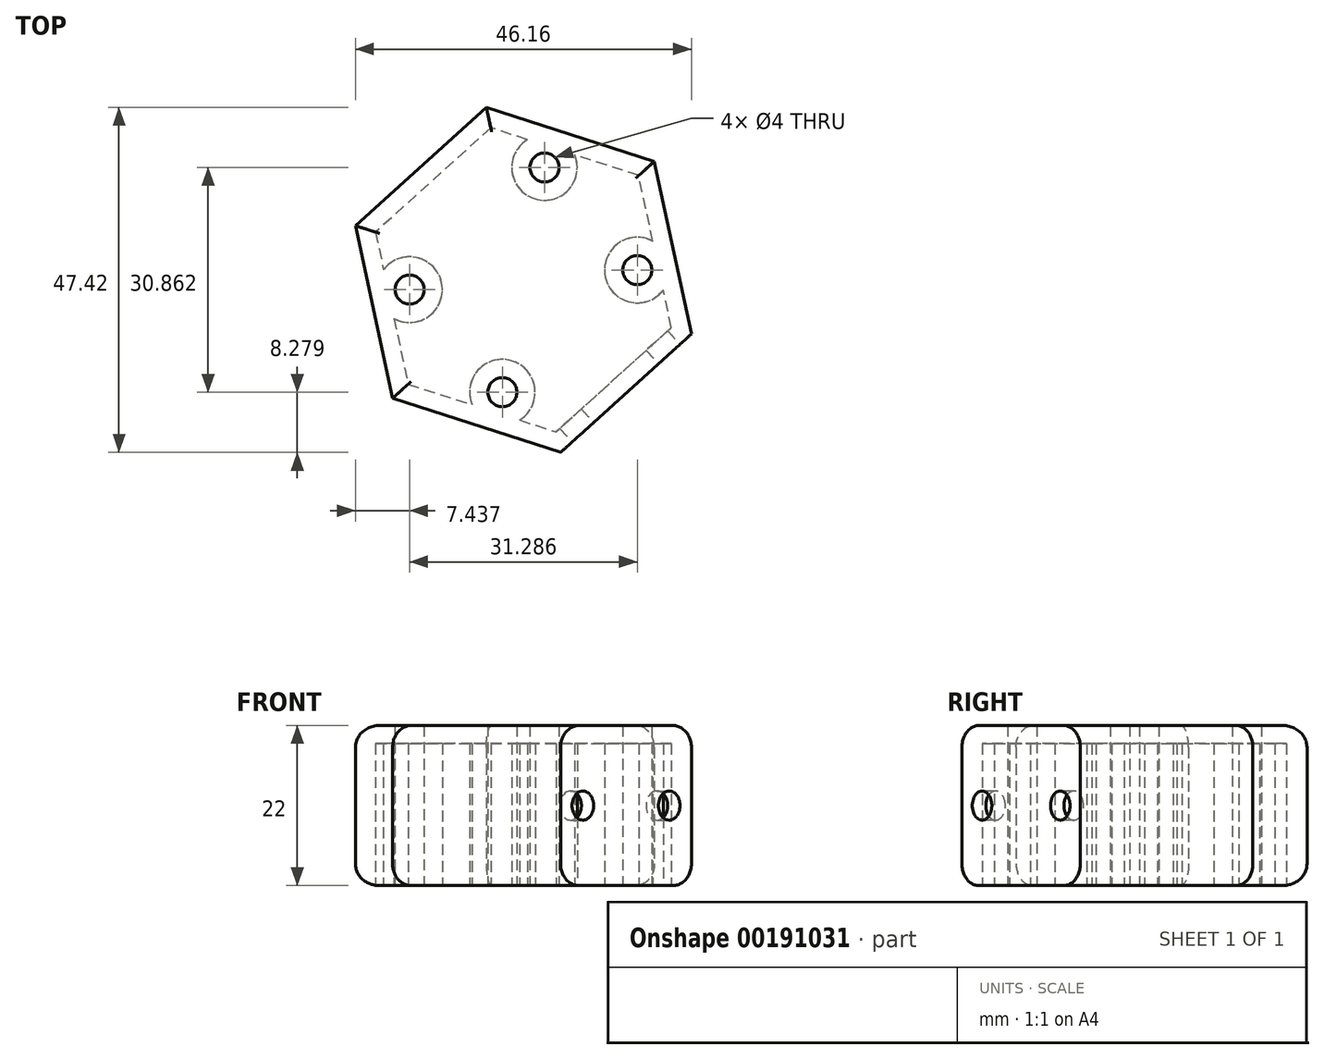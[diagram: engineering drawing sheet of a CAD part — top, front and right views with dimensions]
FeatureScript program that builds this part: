
annotation { "Feature Type Name" : "Feature", "Feature Type Description" : "" }
export const myFeature = defineFeature(function(context is Context, id is Id, definition is map)
    precondition{}
    {
        {
            var Q0;
            Q0=qCreatedBy(makeId("Top.planeOp"),FACE);
            var sketch = newSketch(context, id + "F0", { "sketchPlane" : qUnion([Q0])});
            skCircle(sketch, "E0.cCircle", {"center": v(0, 0) * mm, "radius": 21 * mm, "construction": true});
            skLineSegment(sketch, "E0.0", {"start": v(23.08, -7.44) * mm, "end": v(5.1, -23.7) * mm});
            skLineSegment(sketch, "E0.1", {"start": v(5.1, -23.7) * mm, "end": v(-17.98, -16.27) * mm});
            skLineSegment(sketch, "E0.2", {"start": v(-17.98, -16.27) * mm, "end": v(-23.08, 7.44) * mm});
            skLineSegment(sketch, "E0.3", {"start": v(-23.08, 7.44) * mm, "end": v(-5.1, 23.7) * mm});
            skLineSegment(sketch, "E0.4", {"start": v(-5.1, 23.7) * mm, "end": v(17.98, 16.27) * mm});
            skLineSegment(sketch, "E0.5", {"start": v(17.98, 16.27) * mm, "end": v(23.08, -7.44) * mm});
            skPoint(sketch, "E0.0.midPoint", {"position": v(14.09, -15.57) * mm});
            skLineSegment(sketch, "E1", {"start": v(17.98, 16.27) * mm, "end": v(-17.98, -16.27) * mm, "construction": true});
            skLineSegment(sketch, "E2", {"start": v(14.09, -15.57) * mm, "end": v(-14.09, 15.57) * mm, "construction": true});
            skPoint(sketch, "E3", {"position": v(-15.64, -1.34) * mm});
            skPoint(sketch, "E4.MirrorP", {"position": v(2.9, 15.43) * mm});
            skPoint(sketch, "E5.MirrorP", {"position": v(-2.9, -15.43) * mm});
            skPoint(sketch, "E6.MirrorP", {"position": v(15.64, 1.34) * mm});
            skSolve(sketch);
        }
        {
            var Q0;
            Q0=makeQuery(id+"F0.imprint","IMPRINT",FACE,{"disambiguationData":[TD([[makeQuery(id+"F0.imprint","IMPRINT",EDGE,{"derivedFrom":sQuery(id+"F0.wireOp",EDGE,"E0.0")}),-1.0]])]});
            extrude(context, id + "F1", {"entities" : qUnion([Q0]), "depth" : 22 * mm});
        }
        {
            var Q0;
            Q0=sQuery(id+"F0.wireOp",VERTEX,"E4.MirrorP");
            var Q1;
            Q1=sQuery(id+"F0.wireOp",VERTEX,"E3");
            var Q2;
            Q2=sQuery(id+"F0.wireOp",VERTEX,"E5.MirrorP");
            var Q3;
            Q3=sQuery(id+"F0.wireOp",VERTEX,"E6.MirrorP");
            var Q4;
            Q4=makeQuery(id+"F1.opExtrude","SWEPT_BODY",BODY,{"disambiguationData":[OSD([sQuery(id+"F0.wireOp",EDGE,"E0.0"),sQuery(id+"F0.wireOp",EDGE,"E0.1"),sQuery(id+"F0.wireOp",EDGE,"E0.2"),sQuery(id+"F0.wireOp",EDGE,"E0.3"),sQuery(id+"F0.wireOp",EDGE,"E0.4"),sQuery(id+"F0.wireOp",EDGE,"E0.5")])]});
            hole(context, id + "F2", {"style" : HoleStyle.SIMPLE, "endStyle" : HoleEndStyle.THROUGH, "oppositeDirection" : true, "holeDiameter" : 4 * mm, "locations" : qUnion([Q0, Q1, Q2, Q3]), "scope" : qUnion([Q4]), "isTappedThrough" : true});
        }
        {
            var Q0;
            Q0=makeQuery(id+"F1.opExtrude","CAP_FACE",FACE,{"disambiguationData":[OSD([sQuery(id+"F0.wireOp",EDGE,"E0.0"),sQuery(id+"F0.wireOp",EDGE,"E0.1"),sQuery(id+"F0.wireOp",EDGE,"E0.2"),sQuery(id+"F0.wireOp",EDGE,"E0.3"),sQuery(id+"F0.wireOp",EDGE,"E0.4"),sQuery(id+"F0.wireOp",EDGE,"E0.5")])],"isStart":true});
            var Q1;
            Q1=makeQuery(id+"F2.hole-0.boolean.opBoolean","COPY",FACE,{"derivedFrom":makeQuery(id+"F2.hole-0.opRevolve","SWEPT_FACE",FACE,{"disambiguationData":[OSD([sQuery(id+"F2.hole-0.sketch.wireOp",EDGE,"core_line_2")])]})});
            var Q2;
            Q2=makeQuery(id+"F2.hole-3.boolean.opBoolean","COPY",FACE,{"derivedFrom":makeQuery(id+"F2.hole-3.opRevolve","SWEPT_FACE",FACE,{"disambiguationData":[OSD([sQuery(id+"F2.hole-3.sketch.wireOp",EDGE,"core_line_2")])]})});
            var Q3;
            Q3=makeQuery(id+"F2.hole-2.boolean.opBoolean","COPY",FACE,{"derivedFrom":makeQuery(id+"F2.hole-2.opRevolve","SWEPT_FACE",FACE,{"disambiguationData":[OSD([sQuery(id+"F2.hole-2.sketch.wireOp",EDGE,"core_line_2")])]})});
            var Q4;
            Q4=makeQuery(id+"F2.hole-1.boolean.opBoolean","COPY",FACE,{"derivedFrom":makeQuery(id+"F2.hole-1.opRevolve","SWEPT_FACE",FACE,{"disambiguationData":[OSD([sQuery(id+"F2.hole-1.sketch.wireOp",EDGE,"core_line_2")])]})});
            shell(context, id + "F3", {"entities" : qUnion([Q0, Q1, Q2, Q3, Q4]), "thickness" : 2.5 * mm});
        }
        {
            var Q0;
            Q0=makeQuery(id+"F1.opExtrude","SWEPT_FACE",FACE,{"disambiguationData":[OSD([sQuery(id+"F0.wireOp",EDGE,"E0.0")])]});
            var sketch = newSketch(context, id + "F4", { "sketchPlane" : qUnion([Q0])});
            skLineSegment(sketch, "E7.bottom", {"start": v(-12.12, 22) * mm, "end": v(12.12, 22) * mm});
            skLineSegment(sketch, "E7.top", {"start": v(-12.12, 0) * mm, "end": v(12.12, 0) * mm});
            skLineSegment(sketch, "E7.left", {"start": v(-12.12, 22) * mm, "end": v(-12.12, 0) * mm});
            skLineSegment(sketch, "E7.right", {"start": v(12.12, 22) * mm, "end": v(12.12, 0) * mm});
            skLineSegment(sketch, "E8", {"start": v(0, 22) * mm, "end": v(0, 0) * mm, "construction": true});
            skLineSegment(sketch, "E9", {"start": v(-12.12, 11) * mm, "end": v(12.12, 11) * mm, "construction": true});
            skPoint(sketch, "E10", {"position": v(-8, 11) * mm});
            skPoint(sketch, "E11.MirrorP", {"position": v(8, 11) * mm});
            skSolve(sketch);
        }
        {
            var Q0;
            Q0=makeQuery(id+"F1.opExtrude","CAP_EDGE",EDGE,{"disambiguationData":[OSD([sQuery(id+"F0.wireOp",EDGE,"E0.1")])],"isStart":false});
            var Q1;
            Q1=makeQuery(id+"F1.opExtrude","CAP_EDGE",EDGE,{"disambiguationData":[OSD([sQuery(id+"F0.wireOp",EDGE,"E0.2")])],"isStart":false});
            var Q2;
            Q2=makeQuery(id+"F1.opExtrude","CAP_EDGE",EDGE,{"disambiguationData":[OSD([sQuery(id+"F0.wireOp",EDGE,"E0.3")])],"isStart":false});
            var Q3;
            Q3=makeQuery(id+"F1.opExtrude","CAP_EDGE",EDGE,{"disambiguationData":[OSD([sQuery(id+"F0.wireOp",EDGE,"E0.4")])],"isStart":false});
            var Q4;
            Q4=makeQuery(id+"F1.opExtrude","CAP_EDGE",EDGE,{"disambiguationData":[OSD([sQuery(id+"F0.wireOp",EDGE,"E0.5")])],"isStart":false});
            var Q5;
            Q5=makeQuery(id+"F1.opExtrude","CAP_EDGE",EDGE,{"disambiguationData":[OSD([sQuery(id+"F0.wireOp",EDGE,"E0.1")])],"isStart":true});
            var Q6;
            Q6=makeQuery(id+"F1.opExtrude","CAP_EDGE",EDGE,{"disambiguationData":[OSD([sQuery(id+"F0.wireOp",EDGE,"E0.2")])],"isStart":true});
            var Q7;
            Q7=makeQuery(id+"F1.opExtrude","CAP_EDGE",EDGE,{"disambiguationData":[OSD([sQuery(id+"F0.wireOp",EDGE,"E0.3")])],"isStart":true});
            var Q8;
            Q8=makeQuery(id+"F1.opExtrude","CAP_EDGE",EDGE,{"disambiguationData":[OSD([sQuery(id+"F0.wireOp",EDGE,"E0.4")])],"isStart":true});
            var Q9;
            Q9=makeQuery(id+"F1.opExtrude","CAP_EDGE",EDGE,{"disambiguationData":[OSD([sQuery(id+"F0.wireOp",EDGE,"E0.5")])],"isStart":true});
            fillet(context, id + "F5", {"entities" : qUnion([Q0, Q1, Q2, Q3, Q4, Q5, Q6, Q7, Q8, Q9]), "radius" : 3 * mm, "tangentPropagation" : true, "allowEdgeOverflow" : false});
        }
        {
            var Q0;
            Q0=sQuery(id+"F4.wireOp",VERTEX,"E10");
            var Q1;
            Q1=sQuery(id+"F4.wireOp",VERTEX,"E11.MirrorP");
            var Q2;
            Q2=makeQuery(id+"F1.opExtrude","SWEPT_BODY",BODY,{"disambiguationData":[OSD([sQuery(id+"F0.wireOp",EDGE,"E0.0"),sQuery(id+"F0.wireOp",EDGE,"E0.1"),sQuery(id+"F0.wireOp",EDGE,"E0.2"),sQuery(id+"F0.wireOp",EDGE,"E0.3"),sQuery(id+"F0.wireOp",EDGE,"E0.4"),sQuery(id+"F0.wireOp",EDGE,"E0.5")])]});
            hole(context, id + "F6", {"style" : HoleStyle.SIMPLE, "endStyle" : HoleEndStyle.BLIND, "holeDiameter" : 4 * mm, "holeDepth" : 6 * mm, "locations" : qUnion([Q0, Q1]), "scope" : qUnion([Q2])});
        }
    });
